# Revit family: Jewel sofa
name_source: partatom
category: Arredi
units: mm (PartAtom-declared; Revit-internal decimal feet)

## family parameters
Basato su piano di lavoro = No
Condiviso = No
Numero OmniClass = 23.40.20.00
Punto di calcolo locali = No
Sempre verticale = Sì
Taglio con vuoti quando caricato = No
Titolo OmniClass = General Furniture and Specialties

## types (1)
- Jewel sofa
    Assistance = Call for assistance number: 336.941.3446
    Codice assieme = E2020200
    Collection = Jewel
    Commenti sul tipo = Sumptuous curves and ample cushioning
    Depth = 54 mm  [stored 0.177165 ft]
    Descrizione = Wool upholstered wood frame and upholstered wooden base
    Height = 29 mm  [stored 0.0951444 ft]
    Industry = Hospitality Lounge Areas, or anywhere comfortable sofa seating is desired
    Manufacturer Country = USA
    Modello = Jewel Sofa
    Products of collection = Jewel Sofa
    Produttore = Beaufurn
    Prospetto di default = 0 mm  [stored 0 ft]
    Seat height = 16 mm  [stored 0.0524934 ft]
    URL = https://beaufurn.com
    Usage = Indoor
    Wight = 100 mm  [stored 0.328084 ft]
    Yardage = 15

note: [stored X ft] marks values corroborated as IEEE doubles in the binary element streams (Revit-internal decimal feet)
